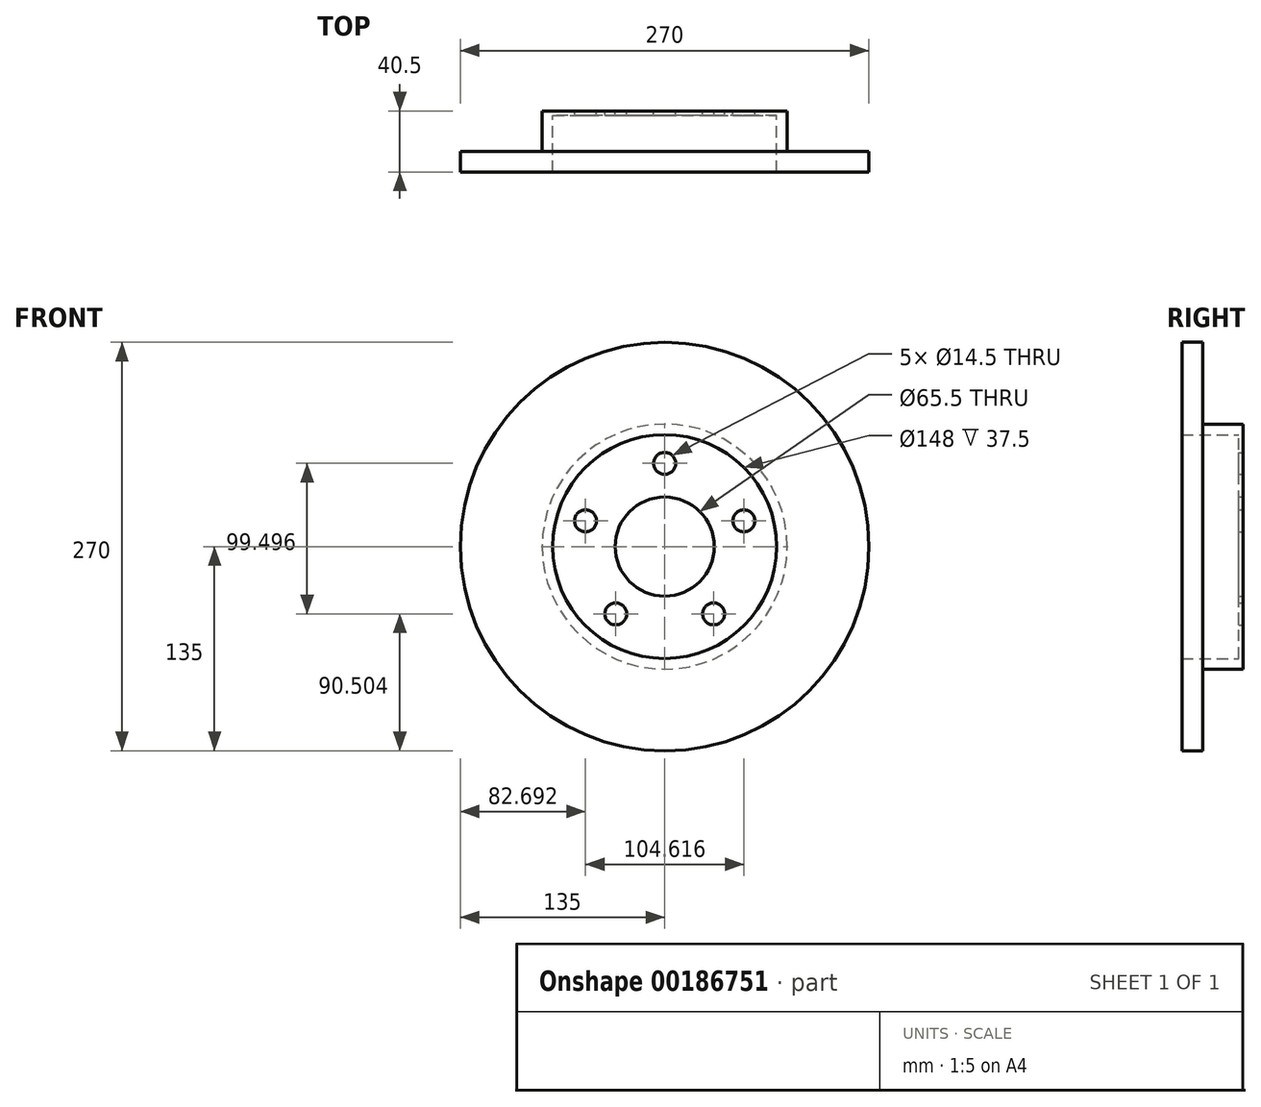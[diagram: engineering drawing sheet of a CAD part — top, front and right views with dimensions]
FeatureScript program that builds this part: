
annotation { "Feature Type Name" : "Feature", "Feature Type Description" : "" }
export const myFeature = defineFeature(function(context is Context, id is Id, definition is map)
    precondition{}
    {
        {
            var Q0;
            Q0=qCreatedBy(makeId("Front.planeOp"),FACE);
            var sketch = newSketch(context, id + "F0", { "sketchPlane" : qUnion([Q0])});
            skCircle(sketch, "E0", {"center": v(0, 0) * mm, "radius": 32.75 * mm});
            skCircle(sketch, "E1", {"center": v(0, 55) * mm, "radius": 7.25 * mm});
            skCircle(sketch, "E2.1.0", {"center": v(-52.3, 17) * mm, "radius": 7.25 * mm});
            skCircle(sketch, "E2.2.0", {"center": v(-32.33, -44.5) * mm, "radius": 7.25 * mm});
            skCircle(sketch, "E2.3.0", {"center": v(32.33, -44.5) * mm, "radius": 7.25 * mm});
            skCircle(sketch, "E2.4.0", {"center": v(52.3, 17) * mm, "radius": 7.25 * mm});
            skCircle(sketch, "E3", {"center": v(0, 0) * mm, "radius": 74 * mm});
            skSolve(sketch);
        }
        {
            var Q0;
            Q0=makeQuery(id+"F0.imprint","IMPRINT",FACE,{"disambiguationData":[TD([[makeQuery(id+"F0.imprint","IMPRINT",EDGE,{"derivedFrom":sQuery(id+"F0.wireOp",EDGE,"E0")}),-1.0]])]});
            extrude(context, id + "F1", {"entities" : qUnion([Q0]), "depth" : 3 * mm});
        }
        {
            var Q0;
            Q0=makeQuery(id+"F1.opExtrude","CAP_FACE",FACE,{"disambiguationData":[OSD([sQuery(id+"F0.wireOp",EDGE,"E0"),sQuery(id+"F0.wireOp",EDGE,"E1"),sQuery(id+"F0.wireOp",EDGE,"E2.1.0"),sQuery(id+"F0.wireOp",EDGE,"E2.2.0"),sQuery(id+"F0.wireOp",EDGE,"E2.3.0"),sQuery(id+"F0.wireOp",EDGE,"E2.4.0"),sQuery(id+"F0.wireOp",EDGE,"E3")])],"isStart":true});
            var sketch = newSketch(context, id + "F2", { "sketchPlane" : qUnion([Q0])});
            skCircle(sketch, "E4", {"center": v(0, 0) * mm, "radius": 74 * mm});
            skCircle(sketch, "E5", {"center": v(0, 0) * mm, "radius": 81 * mm});
            skSolve(sketch);
        }
        {
            var Q0;
            Q0=makeQuery(id+"F2.imprint","IMPRINT",FACE,{"disambiguationData":[TD([[makeQuery(id+"F2.imprint","IMPRINT",EDGE,{"derivedFrom":sQuery(id+"F2.wireOp",EDGE,"E4")}),1.0]])]});
            extrude(context, id + "F3", {"entities" : qUnion([Q0]), "operationType" : NewBodyOperationType.ADD, "oppositeDirection" : true, "depth" : 40.5 * mm});
        }
        {
            var Q0;
            Q0=makeQuery(id+"F3.opExtrude","CAP_FACE",FACE,{"disambiguationData":[OSD([sQuery(id+"F2.wireOp",EDGE,"E4"),sQuery(id+"F2.wireOp",EDGE,"E5")])],"isStart":false});
            var sketch = newSketch(context, id + "F4", { "sketchPlane" : qUnion([Q0])});
            skCircle(sketch, "E6", {"center": v(0, 0) * mm, "radius": 74 * mm});
            skCircle(sketch, "E7", {"center": v(0, 0) * mm, "radius": 135 * mm});
            skSolve(sketch);
        }
        {
            var Q0;
            Q0=makeQuery(id+"F4.imprint","IMPRINT",FACE,{"disambiguationData":[TD([[makeQuery(id+"F4.imprint","IMPRINT",EDGE,{"derivedFrom":sQuery(id+"F4.wireOp",EDGE,"E7")}),1.0]])]});
            extrude(context, id + "F5", {"entities" : qUnion([Q0]), "operationType" : NewBodyOperationType.ADD, "oppositeDirection" : true, "depth" : 13.8 * mm});
        }
    });
